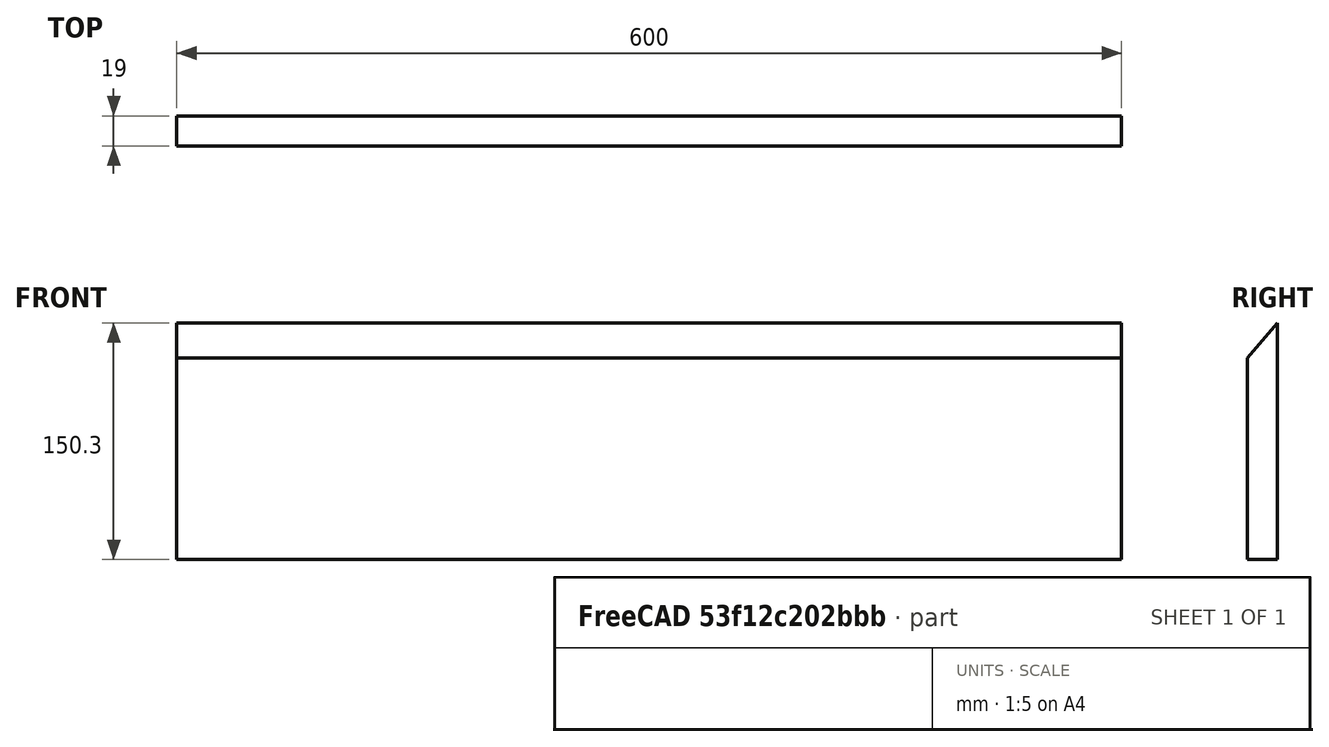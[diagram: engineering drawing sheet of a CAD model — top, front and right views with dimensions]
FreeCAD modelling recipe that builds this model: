
FCSTD DOCUMENT  (FreeCAD 1.0RUnknown)
Label: wardrobe_left_corpus03_jan
License: All rights reserved
objects: TechDraw::DrawViewDimension×4, PartDesign::CoordinateSystem×3, TechDraw::DrawProjGroupItem×2, Sketcher::SketchObject×1, PartDesign::Pad×1, PartDesign::Body×1, App::Part×1, TechDraw::DrawSVGTemplate×1, TechDraw::DrawPage×1
note: 15 computed .brp shape members not serialized (recipe doc carries the construction recipe); baked Part::Feature solids carry a one-line shape summary decoded from their .brp
EXTERNAL_REF file=../../mastersheet.FCStd obj=Spreadsheet
EXTERNAL_REF file=../../mastersketch.FCStd obj=Sketch
EXTERNAL_REF file=../../mastersketch.FCStd obj=Sketch001

FEATURE [Sketcher::SketchObject] Sketch
  ArcFitTolerance = 1e-06
  AttachmentSupport = -> [YZ_Plane]
  FullyConstrained = true
  MakeInternals = false
  MapMode = 5
  Placement = pos=(0,0,0) rot=(0.57735,0.57735,0.57735;2.0944rad)
  expr: Constraints[10] = mastersketch#<<corpus>>.Constraints.corpus03_left_height
  expr: Constraints[6] = mastersheet#Spreadsheet.corpus_outer_thickness
  expr: Constraints[9] = mastersketch#Sketch.Constraints.alpha
  sketch-geometry (4):
    g0: LineSegment StartX=0 StartY=0 StartZ=0 EndX=19 EndY=0 EndZ=0
    g1: LineSegment StartX=19 StartY=0 StartZ=0 EndX=19 EndY=150.296 EndZ=0
    g2: LineSegment StartX=0 StartY=128.064 StartZ=0 EndX=0 EndY=0 EndZ=0
    g3: LineSegment StartX=19 StartY=150.296 StartZ=0 EndX=0 EndY=128.064 EndZ=0
  constraints (12):
    c: Coincident(g0,g1)
    c: Coincident(g2,g0)
    c: Horizontal(g0)
    c: Vertical(g1)
    c: Vertical(g2)
    c: Coincident(g0,g-1)
    c: DistanceX(g0,g0) = 19
    c: Coincident(g3,g1)
    c: Coincident(g2,g3)
    c: Angle(g2,g3) = 2.43442
    c: DistanceY(g2,g2) = 128.064
    c: DistanceY(g1,g1) = 150.296  'max_height'
FEATURE [PartDesign::Pad] Pad
  Direction = (1,0,0)
  Length = 600
  Length2 = 10
  Placement = pos=(0,0,0) rot=(1,1,1;2.0944rad)
  Profile = -> Sketch
  ReferenceAxis = -> Sketch [N_Axis]
  Refine = true
  Suppressed = false
  Type = 0
  expr: Length = mastersheet#Spreadsheet.corpus_depth
FEATURE [PartDesign::Body] Body  label="wardrobe_left_corpus03_jan"
  AllowCompound = false
  Group = -> [Sketch,Pad]
  Origin = -> Origin
  Tip = -> Pad
FEATURE [PartDesign::CoordinateSystem] LCS_1  label="bottom"
  AttacherType = Attacher::AttachEngine3D
  AttachmentSupport = -> [Pad]
  MapMode = 45
  Placement = pos=(300,-6.66e-14,3.33e-14) rot=(0.57735,0.57735,0.57735;2.0944rad)
FEATURE [PartDesign::CoordinateSystem] LCS_2  label="top"
  AttacherType = Attacher::AttachEngine3D
  AttachmentOffset = pos=(0,0,0) rot=(0,0,1;0.863623rad)
  AttachmentSupport = -> [Pad]
  MapMode = 45
  Placement = pos=(300,-5.24e-14,128.064) rot=(0.684188,0.252533,0.684188;2.64687rad)
  expr: .AttachmentOffset.Rotation.Angle = mastersketch#Sketch.Constraints.alpha - 90 °
  expr: .AttachmentOffset.Rotation.Yaw = mastersketch#Sketch.Constraints.alpha - 90 °
FEATURE [PartDesign::CoordinateSystem] LCS_Origin
  AttacherType = Attacher::AttachEngine3D
  AttachmentSupport = -> [X_Axis001]
  MapMode = 2
FEATURE [App::Part] wardrobe_left_corpus03_jan  label="wardrobe_left_corpus03_jan001"
  DrawingName = wardrobe_left_corpus03_jan.FCStd
  Group = -> [LCS_Origin,LCS_1,LCS_2,Body]
  Origin = -> Origin001
  PartDescription = wardrobe_left_corpus03_jan
  PartID = wardrobe_left_corpus03_jan
FEATURE [TechDraw::DrawSVGTemplate] Template  label="Vorlage"
  Height = 210
  Orientation = 1
  Template = <userpath>/scoop/apps/freecad/current/data/Mod/TechDraw/Templates/A4_Landscape_TD.svg
  Width = 297
FEATURE [TechDraw::DrawProjGroupItem] View
  CoarseView = false
  Direction = (0,-1,0)
  Focus = 100
  HardHidden = false
  IsoCount = 0
  IsoHidden = false
  IsoVisible = false
  LockPosition = false
  Perspective = false
  Rotation = 0
  RotationVector = (1,0,0)
  Scale = 0.2
  ScaleType = 2
  ScrubCount = 1
  SeamHidden = false
  SeamVisible = false
  SmoothHidden = false
  SmoothVisible = true
  Source = -> [Body]
  Type = 0
  X = 99.704
  XDirection = (1,0,0)
  Y = 139.979
FEATURE [TechDraw::DrawProjGroupItem] View001
  CoarseView = false
  Direction = (-1,-1e-16,0)
  Focus = 100
  HardHidden = false
  IsoCount = 0
  IsoHidden = false
  IsoVisible = false
  LockPosition = false
  Perspective = false
  Rotation = 0
  RotationVector = (1,0,0)
  Scale = 0.2
  ScaleType = 2
  ScrubCount = 1
  SeamHidden = false
  SeamVisible = false
  SmoothHidden = false
  SmoothVisible = true
  Source = -> [Body]
  Type = 0
  X = 220.732
  XDirection = (1e-16,-1,0)
  Y = 139.979
FEATURE [TechDraw::DrawViewDimension] Dimension  label="Maß"
  AngleOverride = false
  Arbitrary = false
  ArbitraryTolerances = false
  BoxCorners = (2) [(-60,-15.0296,0),(60,15.0296,0)]
  EqualTolerance = true
  ExtensionAngle = 0
  FormatSpec = %.1w
  FormatSpecOverTolerance = %+.1w
  FormatSpecUnderTolerance = %+.1w
  Inverted = false
  LineAngle = 0
  LockPosition = false
  MeasureType = 1
  OverTolerance = 0
  References2D = -> [View]
  Rotation = 0
  ScaleType = 0
  TheoreticalExact = false
  Type = 1
  UnderTolerance = 0
  X = 0
  Y = -21.7911
FEATURE [TechDraw::DrawViewDimension] Dimension001  label="Maß001"
  AngleOverride = false
  Arbitrary = false
  ArbitraryTolerances = false
  BoxCorners = (2) [(-60,-15.0296,0),(60,15.0296,0)]
  EqualTolerance = true
  ExtensionAngle = 0
  FormatSpec = %.1w
  FormatSpecOverTolerance = %+.1w
  FormatSpecUnderTolerance = %+.1w
  Inverted = false
  LineAngle = 0
  LockPosition = false
  MeasureType = 1
  OverTolerance = 0
  References2D = -> [View]
  Rotation = 0
  ScaleType = 0
  TheoreticalExact = false
  Type = 0
  UnderTolerance = 0
  X = 72.8143
  Y = 0
FEATURE [TechDraw::DrawViewDimension] Dimension002  label="Maß002"
  AngleOverride = false
  Arbitrary = false
  ArbitraryTolerances = false
  BoxCorners = (2) [(-1.9,-15.0296,0),(1.9,15.0296,0)]
  EqualTolerance = true
  ExtensionAngle = 0
  FormatSpec = %.1w
  FormatSpecOverTolerance = %+.1w
  FormatSpecUnderTolerance = %+.1w
  Inverted = false
  LineAngle = 0
  LockPosition = false
  MeasureType = 1
  OverTolerance = 0
  References2D = -> [View001]
  Rotation = 0
  ScaleType = 0
  TheoreticalExact = false
  Type = 0
  UnderTolerance = 0
  X = 20.5059
  Y = -26.6941
FEATURE [TechDraw::DrawViewDimension] Dimension003  label="Maß003"
  AngleOverride = false
  Arbitrary = false
  ArbitraryTolerances = false
  BoxCorners = (2) [(-1.9,-15.0296,0),(1.9,15.0296,0)]
  EqualTolerance = true
  ExtensionAngle = 0
  FormatSpec = %.1w
  FormatSpecOverTolerance = %+.1w
  FormatSpecUnderTolerance = %+.1w
  Inverted = false
  LineAngle = 0
  LockPosition = false
  MeasureType = 1
  OverTolerance = 0
  References2D = -> [View001]
  Rotation = 0
  ScaleType = 0
  TheoreticalExact = false
  Type = 6
  UnderTolerance = 0
  X = 28.0714
  Y = 5.82284
FEATURE [TechDraw::DrawPage] Page  label="Seite"
  KeepUpdated = true
  NextBalloonIndex = 1
  ProjectionType = 0
  Template = -> Template
  Views = -> [View,View001,Dimension,Dimension001,Dimension002,Dimension003]
